# Revit family: Paper_Towel_Dispenser_Waste_Receptacle-Bobrick-Fino_Collection-B-9944_Series
name_source: partatom
category: Specialty Equipment
units: mm (PartAtom-declared; Revit-internal decimal feet)

## family parameters
Cut with Voids When Loaded = Yes
Host = Face
OmniClass Number = 23.40.20.21.17
OmniClass Title = Paper Towel Dispensers, Disposal Units
Part Type = Normal
Room Calculation Point = No
Round Connector Dimension = Use Diameter
Shared = Yes

## types (2) — shared parameters
4369-20 Satin Finish Lock and Key = No
4369-20.MBLK Matte Black Lock and Key = No
9944-14 Waste Receptacle Replacement = No
ADA = Yes
ADA Compliant = Yes
Assembly Code = C1030200
Capacity = Paper towel dispenser shall be capable of dispensing 500 C-fold, or 800 multifold paper towels.
Default Elevation = 0"
Depth Of Body = 5"
Description = Semi-Recessed Paper Towel Dispenser and Waste Receptacle
Height = 52"
Inner Frame Width = 11 1/4"
Installation Type = Semi Recessed Wall Mounted
Manufacturer = Bobrick
Minimum Recessed Depth = 4"
Mounting Height = 66"
Paper Towel Dispenser Capacity = 500 C-fold, or 800 multifold paper towels
Rough Wall Opening Depth = 4 1/4"
Rough Wall Opening Height = 51 1/4"
Rough Wall Opening Width = 11 1/2"
URL = https://www.bobrick.com
Waste Container Material = Molded Plastic-Bobrick-Black
Width = 13"

## per-type parameters (varying)
| type | Cabinet Material | Door Material | Material | Paper Towel Dispenser Material |
| B-9944 | Stainless Steel-Bobrick-Satin | Stainless Steel-Bobrick-Satin | Stainless Steel-Bobrick-Satin | Stainless Steel-Bobrick-Satin |
| B-9944.MBLK | Stainless Steel-Bobrick-Matte Black | Stainless Steel-Bobrick-Matte Black | Stainless Steel-Bobrick-Matte Black | Stainless Steel-Bobrick-Matte Black |

note: column(s) folded — value = type name in every type: Model

## geometry (parser evidence)
native form markers: Sweep x3
no freeform markers — native parametric forms only
